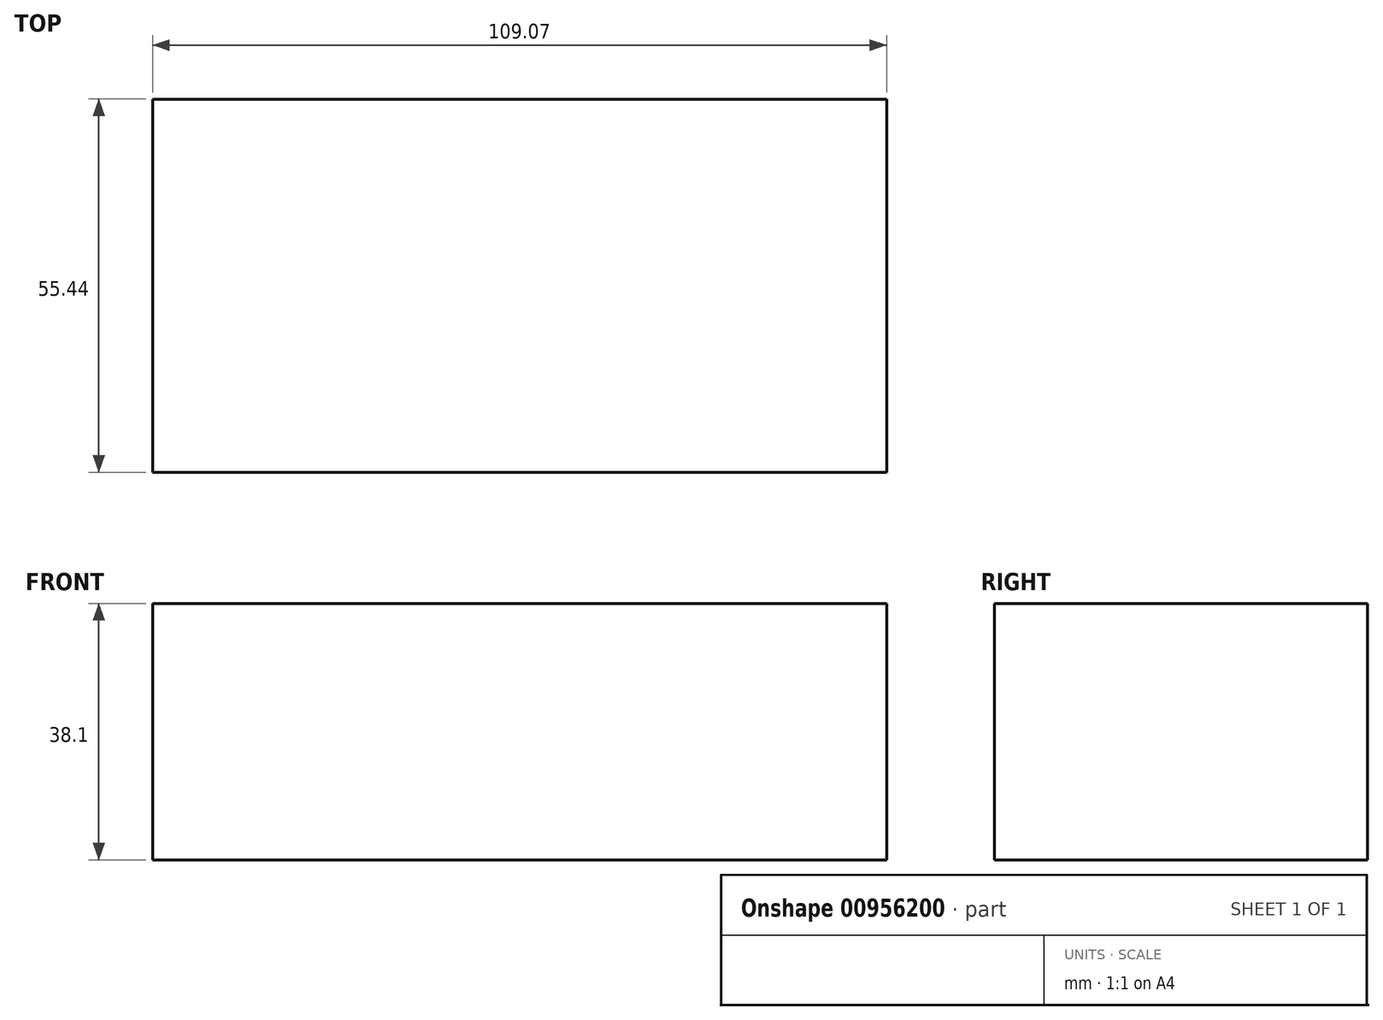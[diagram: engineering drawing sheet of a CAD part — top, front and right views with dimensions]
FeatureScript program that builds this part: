
annotation { "Feature Type Name" : "Feature", "Feature Type Description" : "" }
export const myFeature = defineFeature(function(context is Context, id is Id, definition is map)
    precondition{}
    {
        {
            var Q0;
            Q0=qCreatedBy(makeId("Top.planeOp"),FACE);
            var sketch = newSketch(context, id + "F0", { "sketchPlane" : qUnion([Q0])});
            skLineSegment(sketch, "E0.bottom", {"start": v(-62.55, 0) * mm, "end": v(46.52, 0) * mm});
            skLineSegment(sketch, "E0.top", {"start": v(-62.55, 55.44) * mm, "end": v(46.52, 55.44) * mm});
            skLineSegment(sketch, "E0.left", {"start": v(-62.55, 0) * mm, "end": v(-62.55, 55.44) * mm});
            skLineSegment(sketch, "E0.right", {"start": v(46.52, 0) * mm, "end": v(46.52, 55.44) * mm});
            skSolve(sketch);
        }
        {
            var Q0;
            Q0=makeQuery(id+"F0.imprint","IMPRINT",FACE,{"disambiguationData":[TD([[makeQuery(id+"F0.imprint","IMPRINT",EDGE,{"derivedFrom":sQuery(id+"F0.wireOp",EDGE,"E0.bottom")}),1.0]])]});
            extrude(context, id + "F1", {"entities" : qUnion([Q0]), "depth" : 38.1 * mm, "offsetDistance" : 25.4 * mm});
        }
        {
            var Q0;
            Q0=qCreatedBy(makeId("Right.planeOp"),FACE);
            var sketch = newSketch(context, id + "F2", { "sketchPlane" : qUnion([Q0])});
            skLineSegment(sketch, "E1", {"start": v(24.83, 39.9) * mm, "end": v(35.98, 59.2) * mm});
            skLineSegment(sketch, "E2", {"start": v(35.98, 59.2) * mm, "end": v(13.69, 59.2) * mm});
            skLineSegment(sketch, "E3", {"start": v(13.69, 59.2) * mm, "end": v(24.83, 39.9) * mm});
            skSolve(sketch);
        }
        {
            var Q0;
            Q0 = qSketchRegion(id + "F2", true);
            extrude(context, id + "F3", {"entities" : qUnion([Q0]), "operationType" : NewBodyOperationType.ADD, "depth" : 31.75 * mm, "offsetDistance" : 25.4 * mm});
        }
        {
            var Q0;
            Q0=makeQuery(id+"F3.opExtrude","SWEPT_BODY",BODY,{"disambiguationData":[OSD([sQuery(id+"F2.wireOp",EDGE,"E1"),sQuery(id+"F2.wireOp",EDGE,"E2"),sQuery(id+"F2.wireOp",EDGE,"E3")])]});
            var Q1;
            Q1=makeQuery(id+"F1.opExtrude","SWEPT_BODY",BODY,{"disambiguationData":[OSD([sQuery(id+"F0.wireOp",EDGE,"E0.bottom"),sQuery(id+"F0.wireOp",EDGE,"E0.top"),sQuery(id+"F0.wireOp",EDGE,"E0.left"),sQuery(id+"F0.wireOp",EDGE,"E0.right")])]});
            booleanBodies(context, id + "F4", {"operationType" : BooleanOperationType.SUBTRACTION, "tools" : qUnion([Q0]), "targets" : qUnion([Q1])});
        }
    });
